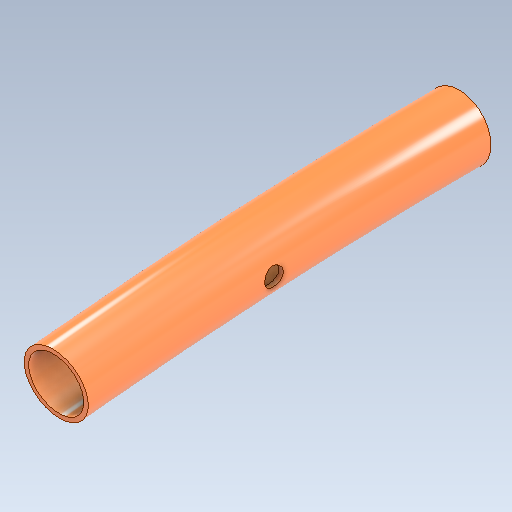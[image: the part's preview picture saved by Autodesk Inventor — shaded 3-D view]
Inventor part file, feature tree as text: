
AUTODESK INVENTOR PART (.ipt)
format: ipt  version: 2021 (Build 250183000, 183)  size: 190,976 bytes
history: native  units: mm
features: sketch x4, extrude x2, revolve x1
ambient origin geometry x8: Origin, YZ Plane, XZ Plane, XY Plane, X Axis, Y Axis, Z Axis, Center Point
bodies: Solid1 (feature_tree)
feature tree (7):
  sketch  "Sketch1"  dims[d0=3300.0mm d1=1650.0mm]
  revolve  "Revolution1"  [1 undecoded]
  extrude  "Extrusion1"  Depth=27.3mm
  extrude  "Extrusion2"  Depth=1.047198mm
  sketch  "Sketch2"  dims[d2=0.0mm d3=27.3mm]
  sketch  "Sketch3"  dims[d4=1.9mm d5=1.047198mm]
  sketch  "Sketch4"  dims[d6=12.0mm d7=0.0mm d8=3300.0mm d9=8.0mm d10=100.0mm d11=0.0mm]
note: 1 required parameter value undecoded (feature->parameter linkage not recoverable at this tier; creation-order binding heuristic only, values carry confidence <= 0.55)
